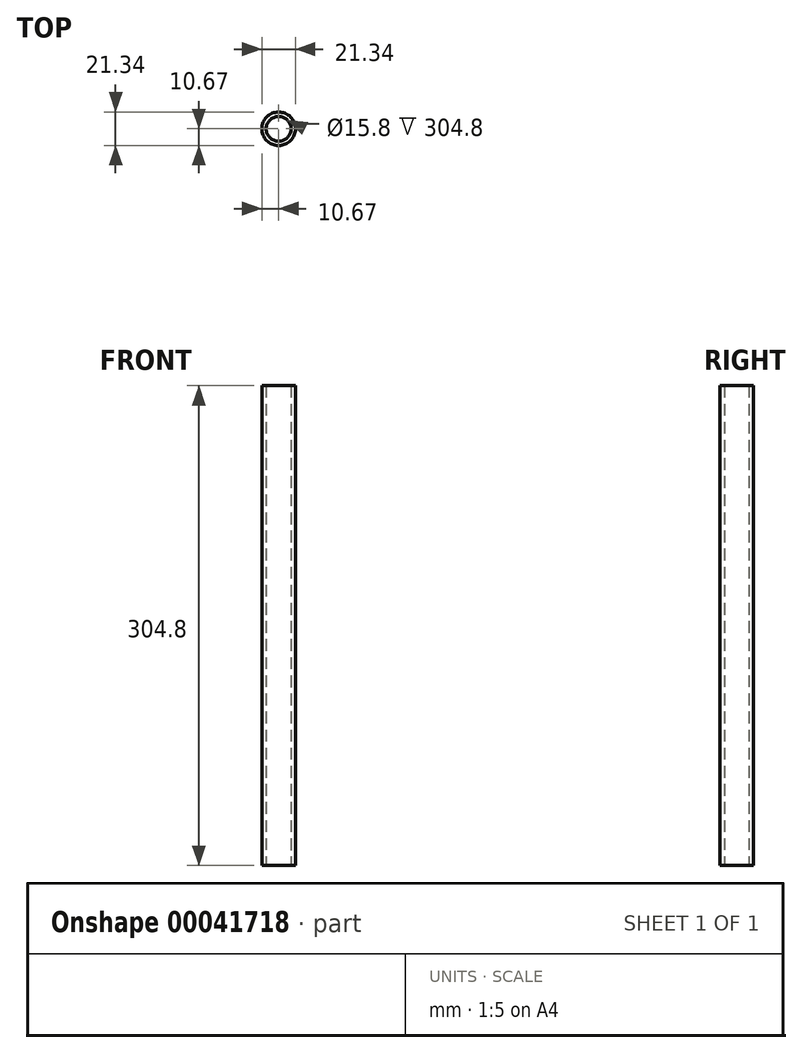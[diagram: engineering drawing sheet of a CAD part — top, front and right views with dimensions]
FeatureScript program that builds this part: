
annotation { "Feature Type Name" : "Feature", "Feature Type Description" : "" }
export const myFeature = defineFeature(function(context is Context, id is Id, definition is map)
    precondition{}
    {
        {
            var Q0;
            Q0=qCreatedBy(makeId("Top.planeOp"),FACE);
            var sketch = newSketch(context, id + "F0", { "sketchPlane" : qUnion([Q0])});
            skCircle(sketch, "E0", {"center": v(0, 0) * mm, "radius": 10.67 * mm});
            skSolve(sketch);
        }
        {
            var Q0;
            Q0 = qSketchRegion(id + "F0", true);
            extrude(context, id + "F1", {"entities" : qUnion([Q0]), "depth" : 304.8 * mm});
        }
        {
            var Q0;
            Q0=qCreatedBy(makeId("Top.planeOp"),FACE);
            var sketch = newSketch(context, id + "F2", { "sketchPlane" : qUnion([Q0])});
            skCircle(sketch, "E1", {"center": v(0, 0) * mm, "radius": 7.9 * mm});
            skSolve(sketch);
        }
        {
            var Q0;
            Q0 = qSketchRegion(id + "F2", true);
            extrude(context, id + "F3", {"entities" : qUnion([Q0]), "operationType" : NewBodyOperationType.REMOVE, "depth" : 304.8 * mm});
        }
    });
